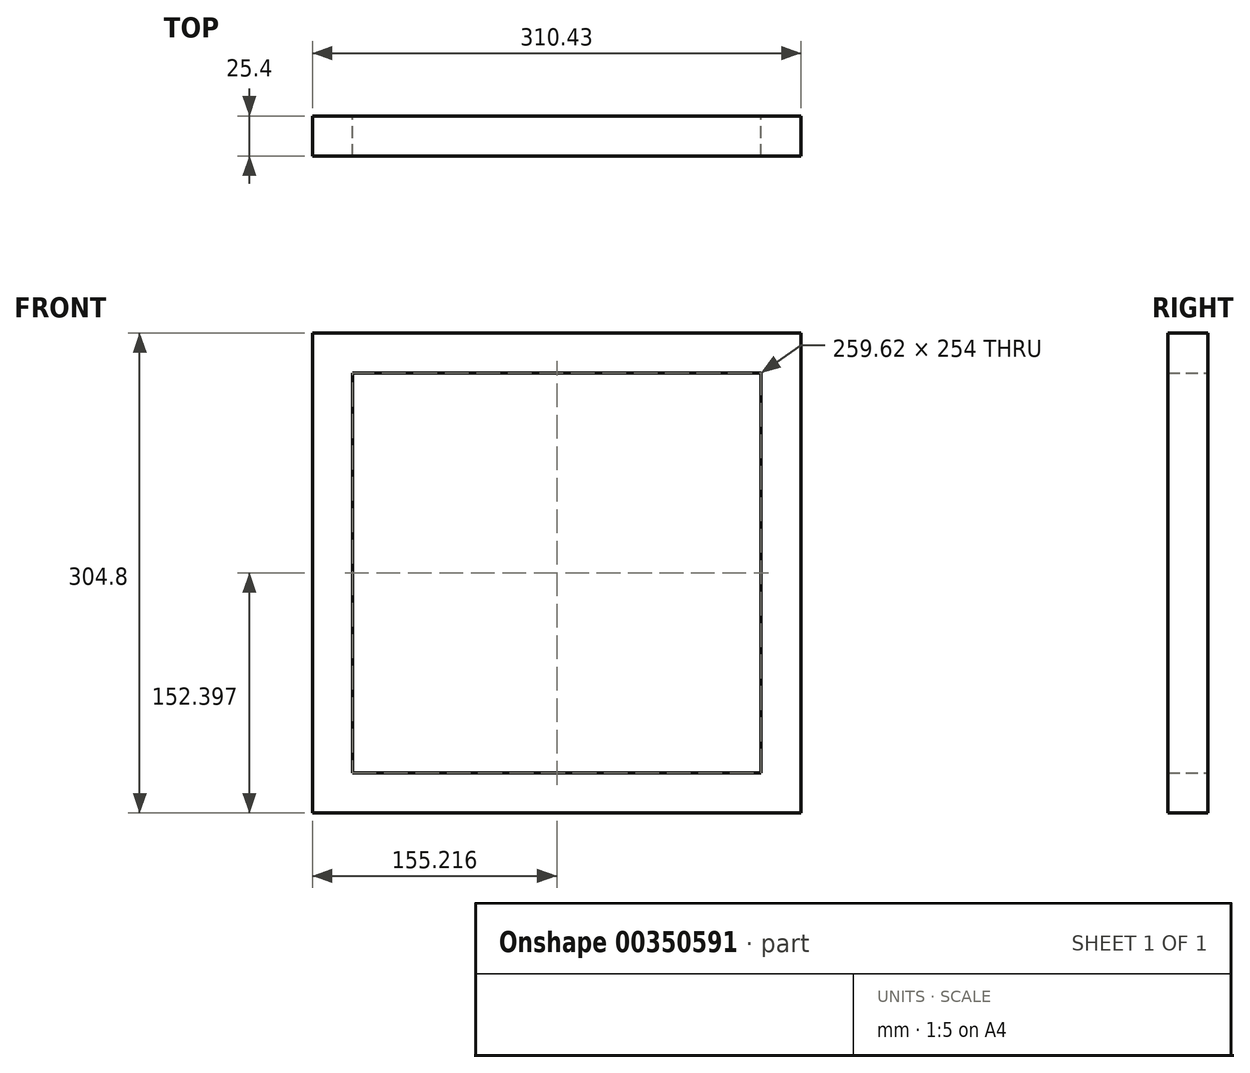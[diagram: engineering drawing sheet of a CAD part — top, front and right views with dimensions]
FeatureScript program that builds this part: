
annotation { "Feature Type Name" : "Feature", "Feature Type Description" : "" }
export const myFeature = defineFeature(function(context is Context, id is Id, definition is map)
    precondition{}
    {
        {
            var Q0;
            Q0=qCreatedBy(makeId("Front.planeOp"),FACE);
            var sketch = newSketch(context, id + "F0", { "sketchPlane" : qUnion([Q0])});
            skLineSegment(sketch, "E0.bottom", {"start": v(153.33, 142.22) * mm, "end": v(-157.1, 142.22) * mm});
            skLineSegment(sketch, "E0.top", {"start": v(153.33, -162.58) * mm, "end": v(-157.1, -162.58) * mm});
            skLineSegment(sketch, "E0.left", {"start": v(153.33, 142.22) * mm, "end": v(153.33, -162.58) * mm});
            skLineSegment(sketch, "E0.right", {"start": v(-157.1, 142.22) * mm, "end": v(-157.1, -162.58) * mm});
            skLineSegment(sketch, "E1.0", {"start": v(127.93, 116.82) * mm, "end": v(-131.7, 116.82) * mm});
            skLineSegment(sketch, "E1.1", {"start": v(127.93, 116.82) * mm, "end": v(127.93, -137.18) * mm});
            skLineSegment(sketch, "E1.2", {"start": v(127.93, -137.18) * mm, "end": v(-131.7, -137.18) * mm});
            skLineSegment(sketch, "E1.3", {"start": v(-131.7, 116.82) * mm, "end": v(-131.7, -137.18) * mm});
            skSolve(sketch);
        }
        {
            var Q0;
            Q0 = qSketchRegion(id + "F0", true);
            extrude(context, id + "F1", {"entities" : qUnion([Q0]), "depth" : 25.4 * mm});
        }
    });
